# Revit family: Deca_Cuba oblonga de apoio_Oval_L.14050
name_source: partatom
category: Plumbing Fixtures
units: mm (PartAtom-declared; Revit-internal decimal feet)

## family parameters
Cut with Voids When Loaded = No
Host = Face
Part Type = Normal
Room Calculation Point = No
Round Connector Dimension = Use Radius
Shared = No

## types (3) — shared parameters
Aprovado por = quattroD
Atendimento ao Cliente = 0800-0117073
Categoria = Cubas
Composição Anel Vedação = -
Composição Assento = -
Composição Básica = Argila; feldspato; caulim; vidrados e corantes inorgânicos.
Composição Componente = Aço inoxidável; elastômeros e plásticos de engenharia.
Consumo = -
Cor Secundária = -
Cores Componente = -
Criado por = quattroD
Código Pai = L.14050
Diâmetro Ponto de Esgoto = 25 mm  [stored 0.082021 ft]
Informações Complementares = -
Itens de Instalação = -
Linha = Oval
Manufacturer = Deca
Norma = NBR-16728-1;NBR-16728-2
Pressão máx. funcionamento = -
Pressão mín. Aquec. Acúmulo = -
Pressão mín. Aquec. Passagem = -
Pressão mín. funcionamento = -
Raio Ponto de Esgoto = 13 mm
Tipo de dispositivo economizador = -
Tipo de mecanismo utilizado = -
Tipo de rosca de entrada = -
Tipo de rosca de saída = -
URL = www.deca.com.br
Vazão na Pressão máx. (L/min) = -
Vazão na Pressão mín. (L/min) = -
zero-valued in all types: Default Elevation

## per-type parameters (varying)
| type | Acompanha o Produto | Cor Interna | Cor Principal | Description | Material | Model | Peso Líquido (Kg) | Saída de Esgoto | Segmento |
| L.14050.22_Marrom Fosco | Retentor Válvula 7701165 ; Folheto cuba squarcle 7920266 ; Tampão Cerâmico para válvula de escoamento (v.14.17.cla); | 22 - Marrom Fosco | 22 - Marrom Fosco | CUBA OBLONGA DE APOIO 50 CM - MARROM FOSCO | Deca_Marrom Fosco | L.14050.22 | 8946 | Válvula Curta | Banheiro Luxo (D43) |
| L.14050.17_Branco | Retentor Válvula 7701165 ; Folheto cuba squarcle 7920266 ; Tampão Cerâmico para válvula de escoamento (v.14.17.cla); | 17 - Branco | 17 - Branco | CUBA OBLONGA DE APOIO 50 CM - BRANCO | Deca_Branco | L.14050.17 | 9166 | - | Banheiro Luxo |
| L.14050.94_Ébano Fosco | Retentor Válvula 7701165 ; Folheto cuba squarcle 7920268 ; Tampão Cerâmico para válvula de escoamento (v.14.17.cla); Fixação SP7 8940007;Ferragem para louça L102L 4317.025.cs; | 94 - Ébano Fosco | 94 - Ébano Fosco | CUBA OBLONGA DE APOIO 50 CM - ÉBANO FOSCO | Deca_Ébano Fosco | L.14050.94 | 8946 | Válvula Curta | Banheiro Luxo (D43) |

note: [stored X ft] marks values corroborated as IEEE doubles in the binary element streams (Revit-internal decimal feet)

## geometry (parser evidence)
native form markers: Sweep x3
no freeform markers — native parametric forms only
